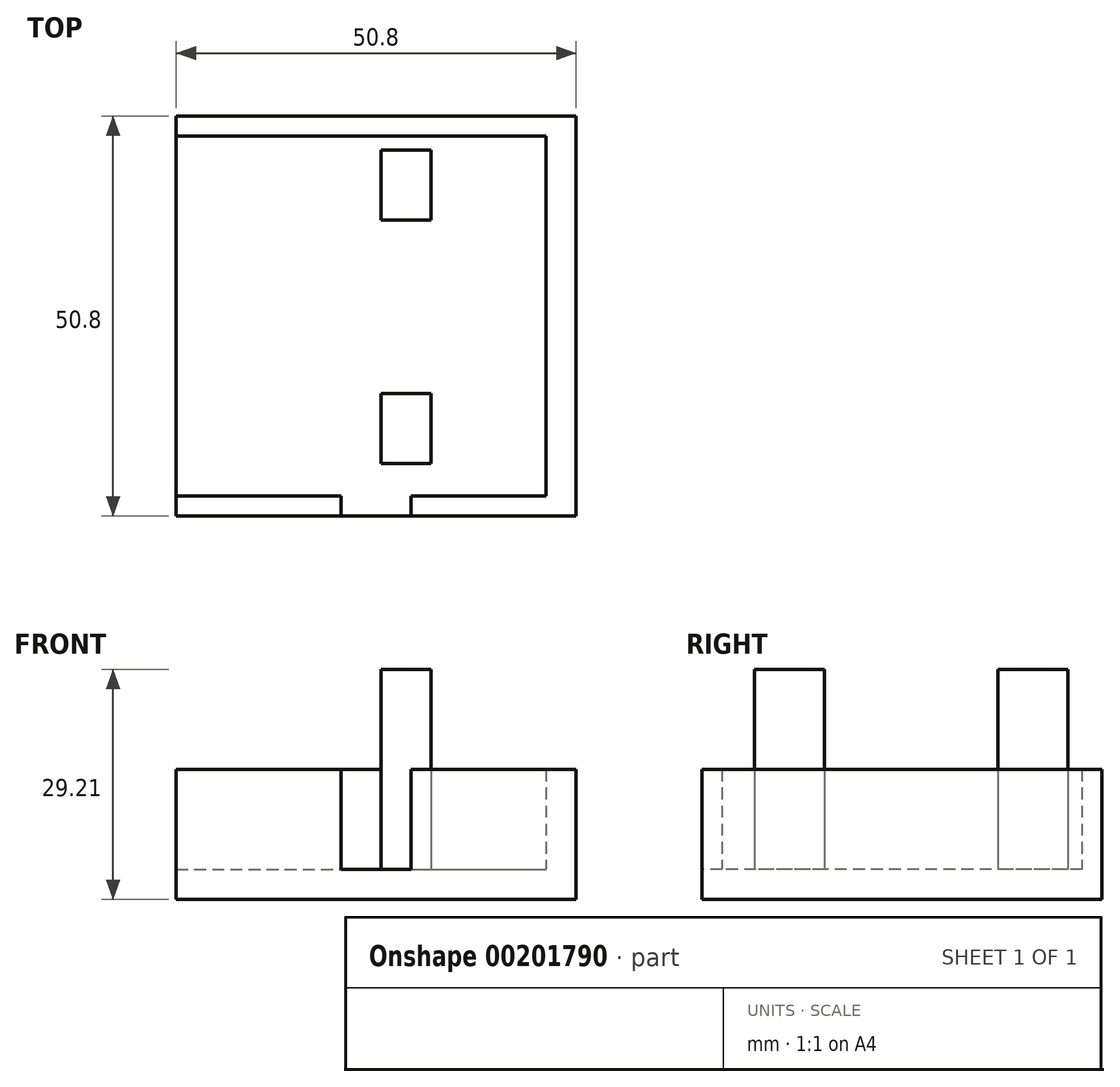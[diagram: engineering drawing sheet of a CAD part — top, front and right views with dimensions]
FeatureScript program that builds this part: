
annotation { "Feature Type Name" : "Feature", "Feature Type Description" : "" }
export const myFeature = defineFeature(function(context is Context, id is Id, definition is map)
    precondition{}
    {
        {
            var Q0;
            Q0=qCreatedBy(makeId("Top.planeOp"),FACE);
            var sketch = newSketch(context, id + "F0", { "sketchPlane" : qUnion([Q0])});
            skLineSegment(sketch, "E0.bottom", {"start": v(-32.01, 32.57) * mm, "end": v(18.79, 32.57) * mm});
            skLineSegment(sketch, "E0.top", {"start": v(-32.01, -18.23) * mm, "end": v(18.79, -18.23) * mm});
            skLineSegment(sketch, "E0.left", {"start": v(-32.01, 32.57) * mm, "end": v(-32.01, -18.23) * mm});
            skLineSegment(sketch, "E0.right", {"start": v(18.79, 32.57) * mm, "end": v(18.79, -18.23) * mm});
            skSolve(sketch);
        }
        {
            var Q0;
            Q0=makeQuery(id+"F0.imprint","IMPRINT",FACE,{"disambiguationData":[TD([[makeQuery(id+"F0.imprint","IMPRINT",EDGE,{"derivedFrom":sQuery(id+"F0.wireOp",EDGE,"E0.bottom")}),-1.0]])]});
            extrude(context, id + "F1", {"entities" : qUnion([Q0]), "depth" : 3.8 * mm});
        }
        {
            var Q0;
            Q0=makeQuery(id+"F1.opExtrude","CAP_FACE",FACE,{"disambiguationData":[OSD([sQuery(id+"F0.wireOp",EDGE,"E0.bottom"),sQuery(id+"F0.wireOp",EDGE,"E0.top"),sQuery(id+"F0.wireOp",EDGE,"E0.left"),sQuery(id+"F0.wireOp",EDGE,"E0.right")])],"isStart":false});
            var sketch = newSketch(context, id + "F2", { "sketchPlane" : qUnion([Q0])});
            skLineSegment(sketch, "E1.bottom", {"start": v(-32.01, 32.57) * mm, "end": v(18.79, 32.57) * mm});
            skLineSegment(sketch, "E1.top", {"start": v(-32.01, 30.03) * mm, "end": v(18.79, 30.03) * mm});
            skLineSegment(sketch, "E1.left", {"start": v(-32.01, 32.57) * mm, "end": v(-32.01, 30.03) * mm});
            skLineSegment(sketch, "E1.right", {"start": v(18.79, 32.57) * mm, "end": v(18.79, 30.03) * mm});
            skSolve(sketch);
        }
        {
            var Q0;
            Q0 = qSketchRegion(id + "F2", true);
            extrude(context, id + "F3", {"entities" : qUnion([Q0]), "operationType" : NewBodyOperationType.ADD, "depth" : 12.7 * mm});
        }
        {
            var Q0;
            Q0=makeQuery(id+"F1.opExtrude","CAP_FACE",FACE,{"disambiguationData":[OSD([sQuery(id+"F0.wireOp",EDGE,"E0.bottom"),sQuery(id+"F0.wireOp",EDGE,"E0.top"),sQuery(id+"F0.wireOp",EDGE,"E0.left"),sQuery(id+"F0.wireOp",EDGE,"E0.right")])],"isStart":false});
            var sketch = newSketch(context, id + "F4", { "sketchPlane" : qUnion([Q0])});
            skLineSegment(sketch, "E2.bottom", {"start": v(-32.01, -15.69) * mm, "end": v(-11.06, -15.69) * mm});
            skLineSegment(sketch, "E2.top", {"start": v(-32.01, -18.23) * mm, "end": v(-11.06, -18.23) * mm});
            skLineSegment(sketch, "E2.left", {"start": v(-32.01, -15.69) * mm, "end": v(-32.01, -18.23) * mm});
            skLineSegment(sketch, "E2.right", {"start": v(-11.06, -15.69) * mm, "end": v(-11.06, -18.23) * mm});
            skSolve(sketch);
        }
        {
            var Q0;
            Q0 = qSketchRegion(id + "F4", true);
            extrude(context, id + "F5", {"entities" : qUnion([Q0]), "operationType" : NewBodyOperationType.ADD, "depth" : 12.7 * mm});
        }
        {
            var Q0;
            Q0=makeQuery(id+"F1.opExtrude","CAP_FACE",FACE,{"disambiguationData":[OSD([sQuery(id+"F0.wireOp",EDGE,"E0.bottom"),sQuery(id+"F0.wireOp",EDGE,"E0.top"),sQuery(id+"F0.wireOp",EDGE,"E0.left"),sQuery(id+"F0.wireOp",EDGE,"E0.right")])],"isStart":false});
            var sketch = newSketch(context, id + "F6", { "sketchPlane" : qUnion([Q0])});
            skLineSegment(sketch, "E3.bottom", {"start": v(-2.17, -15.69) * mm, "end": v(18.79, -15.69) * mm});
            skLineSegment(sketch, "E3.top", {"start": v(-2.17, -18.23) * mm, "end": v(18.79, -18.23) * mm});
            skLineSegment(sketch, "E3.left", {"start": v(-2.17, -15.69) * mm, "end": v(-2.17, -18.23) * mm});
            skLineSegment(sketch, "E3.right", {"start": v(18.79, -15.69) * mm, "end": v(18.79, -18.23) * mm});
            skSolve(sketch);
        }
        {
            var Q0;
            Q0 = qSketchRegion(id + "F6", true);
            extrude(context, id + "F7", {"entities" : qUnion([Q0]), "operationType" : NewBodyOperationType.ADD, "depth" : 2.54 * mm});
        }
        {
            var Q0;
            Q0=makeQuery(id+"F1.opExtrude","CAP_FACE",FACE,{"disambiguationData":[OSD([sQuery(id+"F0.wireOp",EDGE,"E0.bottom"),sQuery(id+"F0.wireOp",EDGE,"E0.top"),sQuery(id+"F0.wireOp",EDGE,"E0.left"),sQuery(id+"F0.wireOp",EDGE,"E0.right")])],"isStart":false});
            var sketch = newSketch(context, id + "F8", { "sketchPlane" : qUnion([Q0])});
            skLineSegment(sketch, "E4.bottom", {"start": v(14.98, 30.03) * mm, "end": v(18.79, 30.03) * mm});
            skLineSegment(sketch, "E4.top", {"start": v(14.98, -15.69) * mm, "end": v(18.79, -15.69) * mm});
            skLineSegment(sketch, "E4.left", {"start": v(14.98, 30.03) * mm, "end": v(14.98, -15.69) * mm});
            skLineSegment(sketch, "E4.right", {"start": v(18.79, 30.03) * mm, "end": v(18.79, -15.69) * mm});
            skSolve(sketch);
        }
        {
            var Q0;
            Q0 = qSketchRegion(id + "F8", true);
            extrude(context, id + "F9", {"entities" : qUnion([Q0]), "operationType" : NewBodyOperationType.ADD, "depth" : 2.54 * mm});
        }
        {
            var Q0;
            Q0=makeQuery(id+"F9.boolean.opBoolean","MERGE",FACE,{"derivedFrom":[makeQuery(id+"F3.opExtrude","CAP_FACE",FACE,{"disambiguationData":[OSD([sQuery(id+"F2.wireOp",EDGE,"E1.bottom"),sQuery(id+"F2.wireOp",EDGE,"E1.top"),sQuery(id+"F2.wireOp",EDGE,"E1.left"),sQuery(id+"F2.wireOp",EDGE,"E1.right")])],"isStart":false}),makeQuery(id+"F7.opExtrude","CAP_FACE",FACE,{"disambiguationData":[OSD([sQuery(id+"F6.wireOp",EDGE,"E3.bottom"),sQuery(id+"F6.wireOp",EDGE,"E3.top"),sQuery(id+"F6.wireOp",EDGE,"E3.left"),sQuery(id+"F6.wireOp",EDGE,"E3.right")])],"isStart":false}),makeQuery(id+"F9.opExtrude","CAP_FACE",FACE,{"disambiguationData":[OSD([sQuery(id+"F8.wireOp",EDGE,"E4.bottom"),sQuery(id+"F8.wireOp",EDGE,"E4.top"),sQuery(id+"F8.wireOp",EDGE,"E4.left"),sQuery(id+"F8.wireOp",EDGE,"E4.right")])],"isStart":false})]});
            extrude(context, id + "F10", {"entities" : qUnion([Q0]), "operationType" : NewBodyOperationType.ADD, "depth" : 10.16 * mm});
        }
        {
            var Q0;
            Q0=makeQuery(id+"F1.opExtrude","CAP_FACE",FACE,{"disambiguationData":[OSD([sQuery(id+"F0.wireOp",EDGE,"E0.bottom"),sQuery(id+"F0.wireOp",EDGE,"E0.top"),sQuery(id+"F0.wireOp",EDGE,"E0.left"),sQuery(id+"F0.wireOp",EDGE,"E0.right")])],"isStart":false});
            var sketch = newSketch(context, id + "F11", { "sketchPlane" : qUnion([Q0])});
            skLineSegment(sketch, "E5.bottom", {"start": v(-5.98, -2.68) * mm, "end": v(0.37, -2.68) * mm});
            skLineSegment(sketch, "E5.top", {"start": v(-5.98, -11.57) * mm, "end": v(0.37, -11.57) * mm});
            skLineSegment(sketch, "E5.left", {"start": v(-5.98, -2.68) * mm, "end": v(-5.98, -11.57) * mm});
            skLineSegment(sketch, "E5.right", {"start": v(0.37, -2.68) * mm, "end": v(0.37, -11.57) * mm});
            skSolve(sketch);
        }
        {
            var Q0;
            Q0 = qSketchRegion(id + "F11", true);
            extrude(context, id + "F12", {"entities" : qUnion([Q0]), "operationType" : NewBodyOperationType.ADD, "depth" : 25.4 * mm});
        }
        {
            var Q0;
            Q0=makeQuery(id+"F1.opExtrude","CAP_FACE",FACE,{"disambiguationData":[OSD([sQuery(id+"F0.wireOp",EDGE,"E0.bottom"),sQuery(id+"F0.wireOp",EDGE,"E0.top"),sQuery(id+"F0.wireOp",EDGE,"E0.left"),sQuery(id+"F0.wireOp",EDGE,"E0.right")])],"isStart":false});
            var sketch = newSketch(context, id + "F13", { "sketchPlane" : qUnion([Q0])});
            skLineSegment(sketch, "E6.bottom", {"start": v(-5.98, 28.25) * mm, "end": v(0.37, 28.25) * mm});
            skLineSegment(sketch, "E6.top", {"start": v(-5.98, 19.36) * mm, "end": v(0.37, 19.36) * mm});
            skLineSegment(sketch, "E6.left", {"start": v(-5.98, 28.25) * mm, "end": v(-5.98, 19.36) * mm});
            skLineSegment(sketch, "E6.right", {"start": v(0.37, 28.25) * mm, "end": v(0.37, 19.36) * mm});
            skSolve(sketch);
        }
        {
            var Q0;
            Q0 = qSketchRegion(id + "F13", true);
            extrude(context, id + "F14", {"entities" : qUnion([Q0]), "operationType" : NewBodyOperationType.ADD, "depth" : 25.4 * mm});
        }
    });
